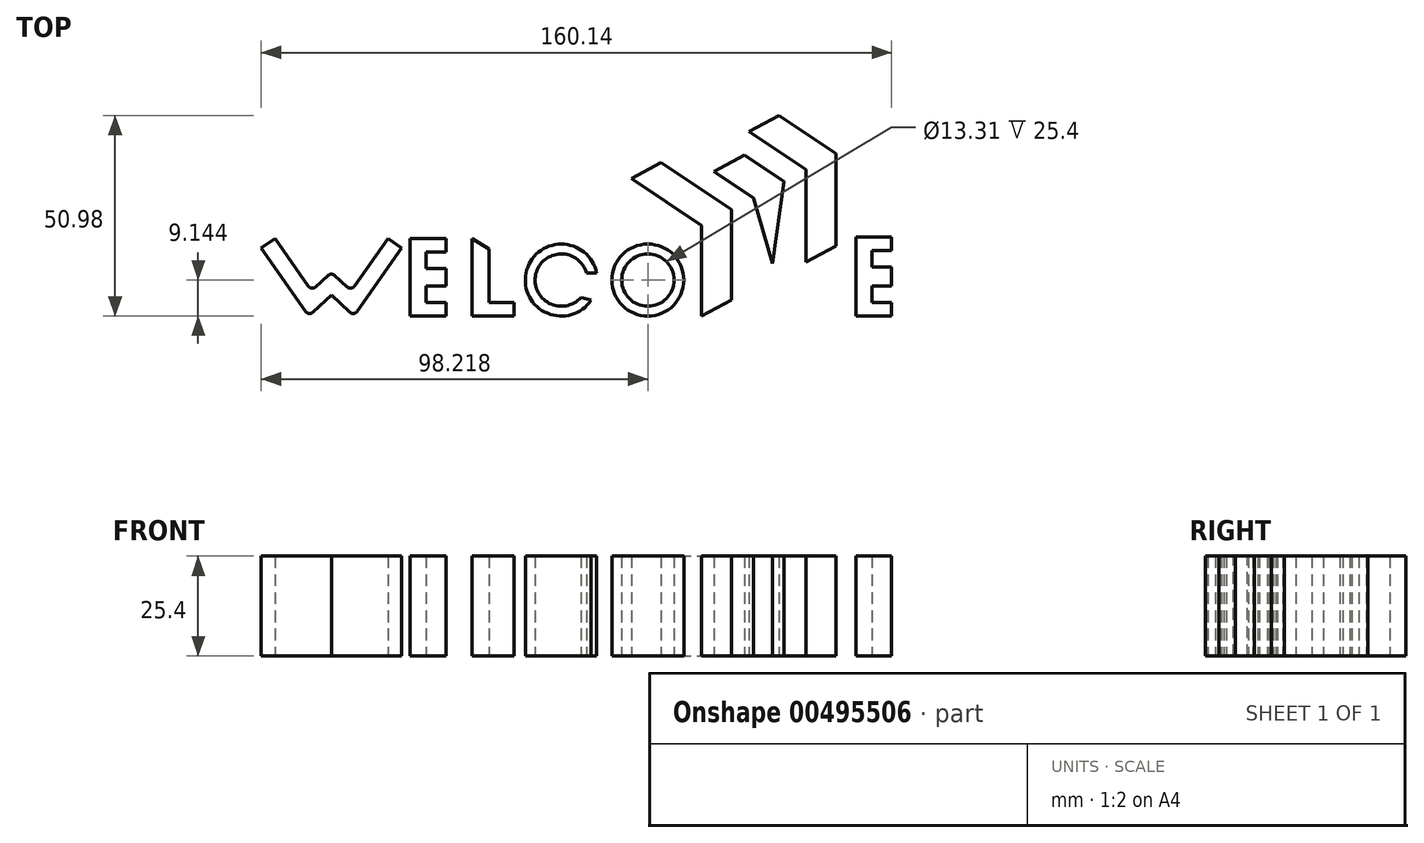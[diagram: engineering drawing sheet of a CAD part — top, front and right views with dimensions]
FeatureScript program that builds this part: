
annotation { "Feature Type Name" : "Feature", "Feature Type Description" : "" }
export const myFeature = defineFeature(function(context is Context, id is Id, definition is map)
    precondition{}
    {
        {
            var Q0;
            Q0=qCreatedBy(makeId("Top.planeOp"),FACE);
            var sketch = newSketch(context, id + "F0", { "sketchPlane" : qUnion([Q0])});
            skLineSegment(sketch, "E0", {"start": v(-59.7, 17.26) * mm, "end": v(-47.61, 0) * mm});
            skLineSegment(sketch, "E1", {"start": v(-47.61, 0) * mm, "end": v(-41.89, 5.31) * mm});
            skLineSegment(sketch, "E2", {"start": v(-21.84, 19.7) * mm, "end": v(-21.84, 0) * mm});
            skLineSegment(sketch, "E3", {"start": v(-21.84, 0) * mm, "end": v(-12.78, 0) * mm});
            skLineSegment(sketch, "E4", {"start": v(-12.78, 0) * mm, "end": v(-12.78, 3.44) * mm});
            skLineSegment(sketch, "E5", {"start": v(-12.78, 3.44) * mm, "end": v(-17.83, 3.44) * mm});
            skLineSegment(sketch, "E6", {"start": v(-17.83, 3.44) * mm, "end": v(-17.83, 7.63) * mm});
            skLineSegment(sketch, "E7", {"start": v(-17.83, 7.63) * mm, "end": v(-12.78, 7.63) * mm});
            skLineSegment(sketch, "E8", {"start": v(-12.78, 7.63) * mm, "end": v(-12.78, 12.12) * mm});
            skLineSegment(sketch, "E9", {"start": v(-12.78, 12.12) * mm, "end": v(-17.83, 12.12) * mm});
            skLineSegment(sketch, "E10", {"start": v(-17.83, 12.12) * mm, "end": v(-17.83, 16.3) * mm});
            skLineSegment(sketch, "E11", {"start": v(-17.83, 16.3) * mm, "end": v(-12.78, 16.3) * mm});
            skLineSegment(sketch, "E12", {"start": v(-12.78, 16.3) * mm, "end": v(-12.78, 19.7) * mm});
            skLineSegment(sketch, "E13", {"start": v(-12.78, 19.7) * mm, "end": v(-21.84, 19.7) * mm});
            skLineSegment(sketch, "E14", {"start": v(-6.14, 19.7) * mm, "end": v(-6.14, 0) * mm});
            skLineSegment(sketch, "E15", {"start": v(-6.14, 0) * mm, "end": v(4.47, 0) * mm});
            skLineSegment(sketch, "E16", {"start": v(4.47, 0) * mm, "end": v(4.47, 3.44) * mm});
            skLineSegment(sketch, "E17", {"start": v(4.47, 3.44) * mm, "end": v(-1.9, 3.44) * mm});
            skLineSegment(sketch, "E18", {"start": v(-1.9, 3.44) * mm, "end": v(-1.9, 17.02) * mm});
            skLineSegment(sketch, "E19", {"start": v(-1.9, 17.02) * mm, "end": v(-6.14, 19.7) * mm});
            skArc(sketch, "E20", {"start": v(25.49, 10.94) * mm, "mid": v(7.56, 10.95) * mm, "end": v(24.1, 4.01) * mm});
            skLineSegment(sketch, "E21", {"start": v(25.49, 10.94) * mm, "end": v(22.94, 10.88) * mm});
            skLineSegment(sketch, "E22", {"start": v(21.5, 4.73) * mm, "end": v(24.1, 4.01) * mm});
            skArc(sketch, "E23", {"start": v(22.94, 10.88) * mm, "mid": v(10.05, 10.67) * mm, "end": v(21.5, 4.73) * mm});
            skCircle(sketch, "E24", {"center": v(38.52, 9.14) * mm, "radius": 9.14 * mm});
            skLineSegment(sketch, "E25", {"start": v(52.14, 0) * mm, "end": v(52.14, 22.98) * mm});
            skLineSegment(sketch, "E26", {"start": v(52.14, 22.98) * mm, "end": v(34.31, 34.9) * mm});
            skLineSegment(sketch, "E27", {"start": v(34.31, 34.9) * mm, "end": v(41.86, 39.01) * mm});
            skLineSegment(sketch, "E28", {"start": v(41.86, 39.01) * mm, "end": v(59.76, 27.05) * mm});
            skLineSegment(sketch, "E29", {"start": v(55.36, 36.7) * mm, "end": v(65.34, 30.03) * mm});
            skLineSegment(sketch, "E30", {"start": v(65.34, 30.03) * mm, "end": v(70.24, 13.3) * mm});
            skLineSegment(sketch, "E31", {"start": v(70.24, 13.3) * mm, "end": v(73.14, 34.2) * mm});
            skLineSegment(sketch, "E32", {"start": v(73.14, 34.2) * mm, "end": v(63.09, 40.92) * mm});
            skLineSegment(sketch, "E33", {"start": v(63.09, 40.92) * mm, "end": v(55.36, 36.7) * mm});
            skLineSegment(sketch, "E34", {"start": v(59.76, 27.05) * mm, "end": v(59.76, 4.07) * mm});
            skLineSegment(sketch, "E35", {"start": v(59.76, 4.07) * mm, "end": v(52.14, 0) * mm});
            skLineSegment(sketch, "E36", {"start": v(59.76, 27.05) * mm, "end": v(105.54, 51.5) * mm, "construction": true});
            skLineSegment(sketch, "E37", {"start": v(64.25, 46.87) * mm, "end": v(78.73, 37.18) * mm});
            skLineSegment(sketch, "E38", {"start": v(78.73, 37.18) * mm, "end": v(78.73, 13.77) * mm});
            skLineSegment(sketch, "E39", {"start": v(78.73, 13.77) * mm, "end": v(86.35, 17.84) * mm});
            skLineSegment(sketch, "E40", {"start": v(86.35, 17.84) * mm, "end": v(86.35, 41.25) * mm});
            skLineSegment(sketch, "E41", {"start": v(86.35, 41.25) * mm, "end": v(71.8, 50.98) * mm});
            skLineSegment(sketch, "E42", {"start": v(71.8, 50.98) * mm, "end": v(64.25, 46.87) * mm});
            skLineSegment(sketch, "E43", {"start": v(-41.89, 5.31) * mm, "end": v(-41.89, -16.01) * mm, "construction": true});
            skLineSegment(sketch, "E44", {"start": v(-41.89, -16.01) * mm, "end": v(-41.89, 5.31) * mm, "construction": true});
            skLineSegment(sketch, "E45", {"start": v(-41.89, 41.54) * mm, "end": v(-41.89, 5.31) * mm, "construction": true});
            skLineSegment(sketch, "E46", {"start": v(-59.7, 17.26) * mm, "end": v(-56.23, 19.7) * mm});
            skLineSegment(sketch, "E47", {"start": v(-56.23, 19.7) * mm, "end": v(-46.93, 6.42) * mm});
            skLineSegment(sketch, "E48", {"start": v(-46.93, 6.42) * mm, "end": v(-41.89, 11.1) * mm});
            skLineSegment(sketch, "E49.MirrorCS", {"start": v(-24.07, 17.26) * mm, "end": v(-36.16, 0) * mm});
            skLineSegment(sketch, "E50.MirrorCS", {"start": v(-24.07, 17.26) * mm, "end": v(-27.55, 19.7) * mm});
            skLineSegment(sketch, "E51.MirrorCS", {"start": v(-27.55, 19.7) * mm, "end": v(-36.84, 6.42) * mm});
            skLineSegment(sketch, "E52.MirrorCS", {"start": v(-36.16, 0) * mm, "end": v(-41.89, 5.31) * mm});
            skLineSegment(sketch, "E53.MirrorCS", {"start": v(-36.84, 6.42) * mm, "end": v(-41.89, 11.1) * mm});
            skLineSegment(sketch, "E54", {"start": v(-56.23, 19.7) * mm, "end": v(-27.55, 19.7) * mm, "construction": true});
            skLineSegment(sketch, "E55", {"start": v(-59.1, 0) * mm, "end": v(78.84, 0) * mm, "construction": true});
            skLineSegment(sketch, "E56", {"start": v(-61.79, 19.7) * mm, "end": v(57.26, 19.7) * mm, "construction": true});
            skLineSegment(sketch, "E57", {"start": v(70.24, 13.3) * mm, "end": v(70.24, 6.53) * mm, "construction": true});
            skCircle(sketch, "E58", {"center": v(38.52, 9.14) * mm, "radius": 6.65 * mm});
            skLineSegment(sketch, "E59", {"start": v(91.38, 20.08) * mm, "end": v(91.38, 0) * mm});
            skLineSegment(sketch, "E60", {"start": v(100.44, 0) * mm, "end": v(100.44, 3.44) * mm});
            skLineSegment(sketch, "E61", {"start": v(100.44, 3.44) * mm, "end": v(95.39, 3.44) * mm});
            skLineSegment(sketch, "E62", {"start": v(95.39, 3.44) * mm, "end": v(95.39, 7.63) * mm});
            skLineSegment(sketch, "E63", {"start": v(95.39, 7.63) * mm, "end": v(100.44, 7.63) * mm});
            skLineSegment(sketch, "E64", {"start": v(100.44, 7.63) * mm, "end": v(100.44, 12.5) * mm});
            skLineSegment(sketch, "E65", {"start": v(100.44, 12.5) * mm, "end": v(95.39, 12.5) * mm});
            skLineSegment(sketch, "E66", {"start": v(95.39, 12.5) * mm, "end": v(95.39, 16.7) * mm});
            skLineSegment(sketch, "E67", {"start": v(95.39, 16.7) * mm, "end": v(100.44, 16.7) * mm});
            skLineSegment(sketch, "E68", {"start": v(100.44, 16.7) * mm, "end": v(100.44, 20.08) * mm});
            skLineSegment(sketch, "E69", {"start": v(91.38, 20.08) * mm, "end": v(100.44, 20.08) * mm});
            skLineSegment(sketch, "E70", {"start": v(91.38, 0) * mm, "end": v(100.44, 0) * mm});
            skSolve(sketch);
        }
        {
            var Q0;
            Q0=makeQuery(id+"F0.imprint","IMPRINT",FACE,{"disambiguationData":[TD([[makeQuery(id+"F0.imprint","IMPRINT",EDGE,{"derivedFrom":sQuery(id+"F0.wireOp",EDGE,"E0")}),1.0]])]});
            var Q1;
            Q1=makeQuery(id+"F0.imprint","IMPRINT",FACE,{"disambiguationData":[TD([[makeQuery(id+"F0.imprint","IMPRINT",EDGE,{"derivedFrom":sQuery(id+"F0.wireOp",EDGE,"E2")}),1.0]])]});
            var Q2;
            Q2=makeQuery(id+"F0.imprint","IMPRINT",FACE,{"disambiguationData":[TD([[makeQuery(id+"F0.imprint","IMPRINT",EDGE,{"derivedFrom":sQuery(id+"F0.wireOp",EDGE,"E14")}),1.0]])]});
            var Q3;
            Q3=makeQuery(id+"F0.imprint","IMPRINT",FACE,{"disambiguationData":[TD([[makeQuery(id+"F0.imprint","IMPRINT",EDGE,{"derivedFrom":sQuery(id+"F0.wireOp",EDGE,"E20")}),1.0]])]});
            var Q4;
            Q4=makeQuery(id+"F0.imprint","IMPRINT",FACE,{"disambiguationData":[TD([[makeQuery(id+"F0.imprint","IMPRINT",EDGE,{"derivedFrom":sQuery(id+"F0.wireOp",EDGE,"E24")}),1.0]])]});
            var Q5;
            Q5=makeQuery(id+"F0.imprint","IMPRINT",FACE,{"disambiguationData":[TD([[makeQuery(id+"F0.imprint","IMPRINT",EDGE,{"derivedFrom":sQuery(id+"F0.wireOp",EDGE,"E25")}),-1.0]])]});
            var Q6;
            Q6=makeQuery(id+"F0.imprint","IMPRINT",FACE,{"disambiguationData":[TD([[makeQuery(id+"F0.imprint","IMPRINT",EDGE,{"derivedFrom":sQuery(id+"F0.wireOp",EDGE,"E29")}),1.0]])]});
            var Q7;
            Q7=makeQuery(id+"F0.imprint","IMPRINT",FACE,{"disambiguationData":[TD([[makeQuery(id+"F0.imprint","IMPRINT",EDGE,{"derivedFrom":sQuery(id+"F0.wireOp",EDGE,"E37")}),1.0]])]});
            var Q8;
            Q8=makeQuery(id+"F0.imprint","IMPRINT",FACE,{"disambiguationData":[TD([[makeQuery(id+"F0.imprint","IMPRINT",EDGE,{"derivedFrom":sQuery(id+"F0.wireOp",EDGE,"E59")}),1.0]])]});
            extrude(context, id + "F1", {"entities" : qUnion([Q0, Q1, Q2, Q3, Q4, Q5, Q6, Q7, Q8]), "depth" : 25.4 * mm});
        }
        {
            var Q0;
            Q0=makeQuery(id+"F1.opExtrude","SWEPT_EDGE",EDGE,{"disambiguationData":[OSD([sQuery(id+"F0.wireOp",EDGE,"E49.MirrorCS"),sQuery(id+"F0.wireOp",EDGE,"E52.MirrorCS")])]});
            var Q1;
            Q1=makeQuery(id+"F1.opExtrude","SWEPT_EDGE",EDGE,{"disambiguationData":[OSD([sQuery(id+"F0.wireOp",EDGE,"E0"),sQuery(id+"F0.wireOp",EDGE,"E1")])]});
            var Q2;
            Q2=makeQuery(id+"F1.opExtrude","SWEPT_EDGE",EDGE,{"disambiguationData":[OSD([sQuery(id+"F0.wireOp",EDGE,"E51.MirrorCS"),sQuery(id+"F0.wireOp",EDGE,"E53.MirrorCS")])]});
            var Q3;
            Q3=makeQuery(id+"F1.opExtrude","SWEPT_EDGE",EDGE,{"disambiguationData":[OSD([sQuery(id+"F0.wireOp",EDGE,"E47"),sQuery(id+"F0.wireOp",EDGE,"E48")])]});
            var Q4;
            Q4=makeQuery(id+"F1.opExtrude","SWEPT_EDGE",EDGE,{"disambiguationData":[OSD([sQuery(id+"F0.wireOp",EDGE,"E48"),sQuery(id+"F0.wireOp",EDGE,"E53.MirrorCS")])]});
            fillet(context, id + "F2", {"entities" : qUnion([Q0, Q1, Q2, Q3, Q4]), "radius" : 1.27 * mm, "tangentPropagation" : true, "allowEdgeOverflow" : false});
        }
    });
